# Revit family: 11
name_source: partatom
category: Plumbing Fixtures
units: mm (PartAtom-declared; Revit-internal decimal feet)

## family parameters
Cut with Voids When Loaded = No
Host = Face
OmniClass Number = 23.45.05.21.11.11
OmniClass Title = Water Operated Water Closets
Part Type = Normal
Room Calculation Point = No
Round Connector Dimension = Use Diameter
Shared = Yes

## types (3) — shared parameters
047007-0070A Inlet Spud (furnished with bowl) = Yes
6047.121.002 - Manual Operated Flushometer Valve 1.28 gpf = No
6047.161.002 - Manual Operated Flushometer Valve 1.6 gpf = No
6065.121.002  - DC Power Sensor Operated  Flushometer Valve Selectronic 1.28 gpf = No
6065.161.002 - DC Power Sensor Operated  Flushometer Valve Selectronic 1.6 gpf = No
6065.721.002  - DC Power Sensor Operated  Flushometer Valve Selectronic 1.28/1.1  gpf = No
6065.761.002 - DC Power Sensor Operated  Flushometer Valve Selectronic 1.61/1.1  gpf = No
6067.121.002 - AC Power Sensor Operated  Flushometer Valve Selectronic 1.28 gpf = No
6067.161.002 - AC PowerSensor Operated  Flushometer Valve Selectronic 1.6 gpf = No
6067.721.002 - AC Power Sensor Operated  Flushometer Valve Selectronic 1.28/1.1  gpf = No
6067.761.002 - AC Power Sensor Operated  Flushometer Valve Selectronic 1.61/1.1  gpf = No
ADA Compliant = Yes
Assembly Code = D2010110
Bowl Shape = Elongated
CW Connection = Yes
CWFU = 5
CalGreen Compliant = Yes
Default Elevation = 0"
Finish = Vitreous China-American Standard-020-White
Flush Rate = 1.1 gpf - 1.6 gpf
HW Connection = No
Height = 15"
IAPMO Compliance = Compliance Certifications - Meets or Exceeds the Following Specifications: ASME A112.19.2/CSA B45.1 for Vitreous China Fixtures
Installation Type = Wall Mount
Length = 26"
Manufacturer = American Standard
Material = Vitreous China-American Standard-020-White
Price = Prices may vary. Please consult Manufacturer Representative for most up-to-date price list.
Product Documentation Link = https://americanstandard.box.com
Product Page URL = https://www.americanstandard-us.com
URL = https://www.americanstandard-us.com
Vent Connection = No
WFU = 5
Waste Connection = Yes
Waste Connection Diameter = 2 1/8"
Waste Connection Radius = 1 1/16"
Width = 14"
zero-valued in all types: HWFU

## per-type parameters (varying)
| type | 5901.100 Heavy duty open front less cover | 5905.100 Extra heavy duty open front less cover | Back Spud | Cold Water Connection Diameter | Cold Water Connection Radius | Connection Bottom Spud | Connection Description 1 | Connection Description 2 | Connection Top Spud | Description | Family Parameter | Model | Top Spud |
| 2634101.020 | Yes | Yes | Yes | 1 1/2" | 3/4" | 1 1/2" | 1 1/2" Cold Water Connection |  | 0" | Afwall® Millennium® 1.1 – 1.6 gpf (4.2 – 6.0 Lpf) Back Spud Elongated Wall-Hung Bowl | Toilet-Elongated-Back_Spud-American_Standard-Afwall_Millennium-2634_Series : 2634101.020 | 2634101.020 | No |
| 2257101.020 | No | No | No | 2 1/8" | 1 1/16" | 0" |  | 1 1/2" Cold Water Inlet Connection | 1 1/2" | Afwall® Millennium® 1.1 – 1.6 gpf (4.2 – 6.0 Lpf) Top Spud Elongated Wall-Hung Bowl | Toilet-Elongated-Top_Spud-American_Standard-Afwall_Millennium-2633,2257_Series : 2257101.020 | 2634101.020 | Yes |
| 2633101.020 | Yes | Yes | Yes | 1 1/2" | 3/4" | 1 1/2" | 1 1/2" Cold Water Connection |  | 0" | Afwall® Millennium® 1.1 – 1.6 gpf (4.2 – 6.0 Lpf) Back Spud Elongated Wall-Hung Bowl | Toilet-Elongated-Back_Spud-American_Standard-Afwall_Millennium-2634_Series : 2634101.020 | 2633101.020 | No |

## geometry (parser evidence)
native form markers: Sweep x5
no freeform markers — native parametric forms only
